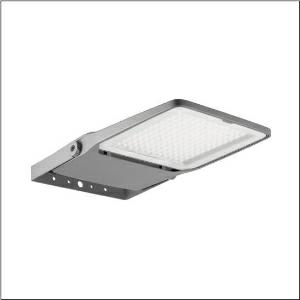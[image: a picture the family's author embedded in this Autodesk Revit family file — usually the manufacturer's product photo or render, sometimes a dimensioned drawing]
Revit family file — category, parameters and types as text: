
# Revit family: floodlight_fl_20_midi___pl61_5xa7682d1c2ac_a0aa
name_source: partatom
category: Lighting Fixtures
units: mm (PartAtom-declared; Revit-internal decimal feet)

## family parameters
Cut with Voids When Loaded = No
Host = Face
Light Source = No
Part Type = Normal
Room Calculation Point = No
Round Connector Dimension = Use Diameter
Shared = No

## types (1)
- --- (1 x LED 3000K / CRI = 80 (unbekannt), 14290 lm, 3000K)
    Apparent Load = 142 VA
    CIE Flux Codes = 33 65 98 100 100
    Color Rendering = 80
    Color Temperature = 3000K
    Default Elevation = 1800 mm
    Description = Floodlight FL 20 midi, floodlight, primary light control with lens, of plastic, primary optical cover: protective disc, of toughened safety glass, transparent, light distribution: PL61, light emission: direct distribution, primary light characteristic: asymmetric, installation type: surface-mounted, LED High Power LED, rated luminous flux: 14.290 lm, light colour: 830, colour temperature: 3000K, control gear: ECG Plus, control: digital communication interface, time-dependent luminous flux control, flexible luminous flux parameterisation, power reduction, overheat protection, electronic power reduction, with terminal, 5-pole, max. 2.5mm², mains connection: 220..240V, AC, 50/60Hz, rated input power: 142W, LED unit, of diecast aluminium, powder-coated, Siteco® metallic grey (DB 702S), length: 731 mm, width: 450 mm, height: 76mm, housing frame, of diecast aluminium, powder-coated, Siteco® metallic grey (DB 702S), wall fastening, of steel, powder-coated, Siteco® metallic grey (DB 702S), DALIprotection rating (complete): IP66, insulation class (complete): insulation class II (safety insulation), certification: CE, ENEC, VDE, protection symbol: D, permissible ambient temperature for indoor applications: -40..+40°C, permissible ambient temperature for outdoor applications: -40..+50°C, standard: DIN EN 12944, packaging unit: 1 piece

Light Distribution: PL61
    Height = 76 mm
    Lamp = 1 x LED 3000K / CRI >= 80 (unbekannt)
    Lamp Light Flux = 14290 lm
    Lamp count = 1
    Length = 731 mm
    Luminous efficacy = 101 lm/W
    Manufacturer = Siteco
    ModVariant = No
    Model = 5XA7682D1C2AC
    Number of Poles = 1
    OnlyDefault = Yes
    Power Factor = 1
    Product Name = Floodlight FL 20 midi | PL61
    Product group = floodlight | pylon top
    ProductGroupID = 6101
    Protection Class = Protection class II
    Protection Degree = IP 66
    RLX_Detail_Level = 1
    RlxData = <blob elided: 91945 chars, md5=1e711006>
    Socket = socket
    Standby Power = 0 W
    System Light Flux = 14290 lm
    System Power = 142 W
    Type Comments = factory setting: luminous flux: 100 % | dim-lin: 254 | 489 mA
    Type Image = l_1005944.jpg
    URL = http://relux.com
    VarID = @adj_142717
    Voltage = 0 V
    Weight = 0.00 kg
    Width = 450 mm

## geometry (parser evidence)
native form markers: Blend x4, Sweep x14
no freeform markers — native parametric forms only
